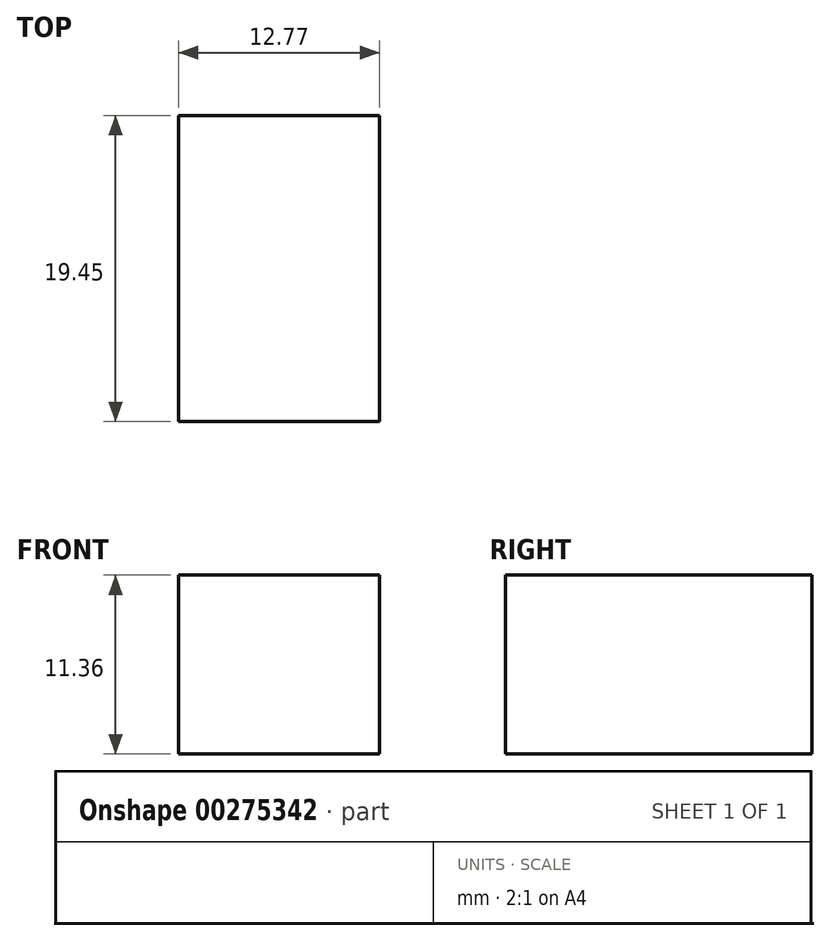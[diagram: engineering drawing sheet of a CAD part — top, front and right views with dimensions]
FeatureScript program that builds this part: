
annotation { "Feature Type Name" : "Feature", "Feature Type Description" : "" }
export const myFeature = defineFeature(function(context is Context, id is Id, definition is map)
    precondition{}
    {
        {
            var Q0;
            Q0=qCreatedBy(makeId("Top.planeOp"),FACE);
            var sketch = newSketch(context, id + "F0", { "sketchPlane" : qUnion([Q0])});
            skLineSegment(sketch, "E0.bottom", {"start": v(0, 0) * mm, "end": v(-12.77, 0) * mm});
            skLineSegment(sketch, "E0.top", {"start": v(0, 19.45) * mm, "end": v(-12.77, 19.45) * mm});
            skLineSegment(sketch, "E0.left", {"start": v(0, 0) * mm, "end": v(0, 19.45) * mm});
            skLineSegment(sketch, "E0.right", {"start": v(-12.77, 0) * mm, "end": v(-12.77, 19.45) * mm});
            skSolve(sketch);
        }
        {
            var Q0;
            Q0=makeQuery(id+"F0.imprint","IMPRINT",FACE,{"disambiguationData":[TD([[makeQuery(id+"F0.imprint","IMPRINT",EDGE,{"derivedFrom":sQuery(id+"F0.wireOp",EDGE,"E0.bottom")}),-1.0]])]});
            extrude(context, id + "F1", {"entities" : qUnion([Q0]), "depth" : 11.36 * mm});
        }
    });
